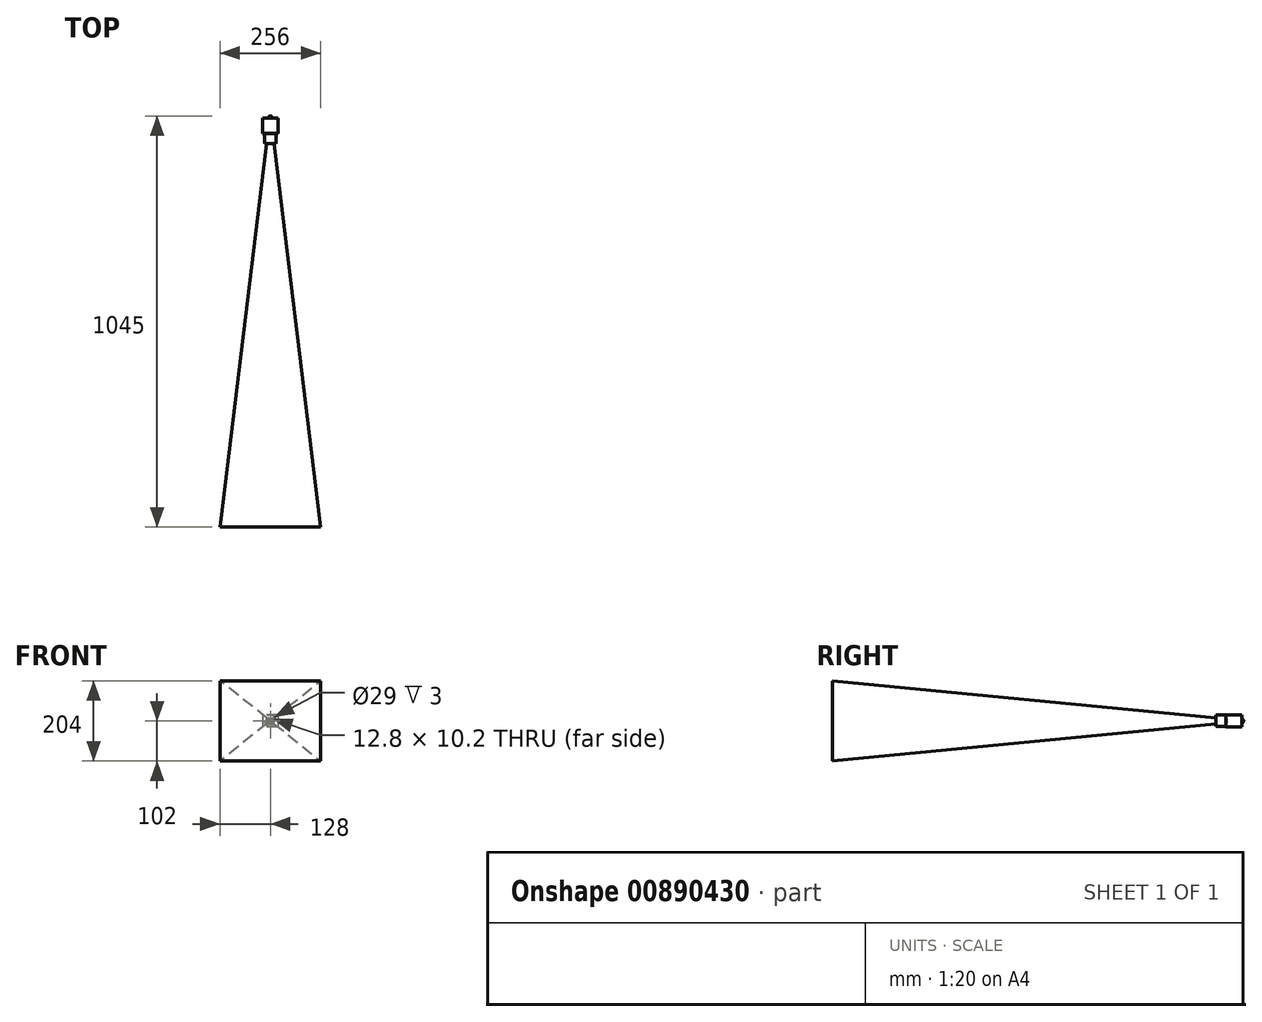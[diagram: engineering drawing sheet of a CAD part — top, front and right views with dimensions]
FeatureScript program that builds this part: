
annotation { "Feature Type Name" : "Feature", "Feature Type Description" : "" }
export const myFeature = defineFeature(function(context is Context, id is Id, definition is map)
    precondition{}
    {
        {
            var Q0;
            Q0=qCreatedBy(makeId("Front.planeOp"),FACE);
            var sketch = newSketch(context, id + "F0", { "sketchPlane" : qUnion([Q0])});
            skLineSegment(sketch, "E0.bottom", {"start": v(20, 15) * mm, "end": v(-20, 15) * mm});
            skLineSegment(sketch, "E0.top", {"start": v(20, -15) * mm, "end": v(-20, -15) * mm});
            skLineSegment(sketch, "E0.left", {"start": v(20, 15) * mm, "end": v(20, -15) * mm});
            skLineSegment(sketch, "E0.right", {"start": v(-20, 15) * mm, "end": v(-20, -15) * mm});
            skPoint(sketch, "E0.middle", {"position": v(0, 0) * mm});
            skSolve(sketch);
        }
        {
            var Q0;
            Q0=qSketchRegion(id+"F0",true);
            extrude(context, id + "F1", {"entities" : qUnion([Q0]), "depth" : 40 * mm, "offsetDistance" : 25 * mm});
        }
        {
            assignVariable(context, id + "F2", {"name" : "WorkingDistance", "anyValue" : 1000});
        }
        {
            var Q0;
            Q0=makeQuery(id+"F1.opExtrude","CAP_FACE",FACE,{"disambiguationData":[OSD([sQuery(id+"F0.wireOp",EDGE,"E0.bottom"),sQuery(id+"F0.wireOp",EDGE,"E0.top"),sQuery(id+"F0.wireOp",EDGE,"E0.left"),sQuery(id+"F0.wireOp",EDGE,"E0.right")])],"isStart":false});
            var sketch = newSketch(context, id + "F3", { "sketchPlane" : qUnion([Q0])});
            skCircle(sketch, "E1", {"center": v(0, 0) * mm, "radius": 14.5 * mm});
            skSolve(sketch);
        }
        {
            var Q0;
            Q0=qSketchRegion(id+"F3",true);
            extrude(context, id + "F4", {"entities" : qUnion([Q0]), "operationType" : NewBodyOperationType.REMOVE, "oppositeDirection" : true, "depth" : 3 * mm, "offsetDistance" : 25 * mm});
        }
        {
            var Q0;
            Q0=makeQuery(id+"F4.boolean.opBoolean","COPY",FACE,{"derivedFrom":makeQuery(id+"F4.opExtrude","CAP_FACE",FACE,{"disambiguationData":[OSD([sQuery(id+"F3.wireOp",EDGE,"E1")])],"isStart":false})});
            var sketch = newSketch(context, id + "F5", { "sketchPlane" : qUnion([Q0])});
            skLineSegment(sketch, "E2.bottom", {"start": v(6.4, 5.1) * mm, "end": v(-6.4, 5.1) * mm});
            skLineSegment(sketch, "E2.top", {"start": v(6.4, -5.1) * mm, "end": v(-6.4, -5.1) * mm});
            skLineSegment(sketch, "E2.left", {"start": v(6.4, 5.1) * mm, "end": v(6.4, -5.1) * mm});
            skLineSegment(sketch, "E2.right", {"start": v(-6.4, 5.1) * mm, "end": v(-6.4, -5.1) * mm});
            skPoint(sketch, "E2.middle", {"position": v(0, 0) * mm});
            skSolve(sketch);
        }
        {
            var Q0;
            Q0=qSketchRegion(id+"F5",true);
            extrude(context, id + "F6", {"entities" : qUnion([Q0]), "operationType" : NewBodyOperationType.ADD, "depth" : 3 * mm, "offsetDistance" : 25 * mm});
        }
        {
            var Q0;
            Q0=makeQuery(id+"F6.opExtrude","CAP_FACE",FACE,{"disambiguationData":[OSD([sQuery(id+"F5.wireOp",EDGE,"E2.bottom"),sQuery(id+"F5.wireOp",EDGE,"E2.top"),sQuery(id+"F5.wireOp",EDGE,"E2.left"),sQuery(id+"F5.wireOp",EDGE,"E2.right")])],"isStart":false});
            cPlane(context, id + "F7", {"entities" : qUnion([Q0]), "cplaneType" : CPlaneType.OFFSET, "offset" : (getVariable(context, 'WorkingDistance')) * mm, "width" : 150 * mm, "height" : 150 * mm});
        }
        {
            var Q0;
            Q0=qCreatedBy(id+"F7.planeOp",FACE);
            var sketch = newSketch(context, id + "F8", { "sketchPlane" : qUnion([Q0])});
            skLineSegment(sketch, "E3.bottom", {"start": v(128, 102) * mm, "end": v(-128, 102) * mm});
            skLineSegment(sketch, "E3.top", {"start": v(128, -102) * mm, "end": v(-128, -102) * mm});
            skLineSegment(sketch, "E3.left", {"start": v(128, 102) * mm, "end": v(128, -102) * mm});
            skLineSegment(sketch, "E3.right", {"start": v(-128, 102) * mm, "end": v(-128, -102) * mm});
            skPoint(sketch, "E3.middle", {"position": v(0, 0) * mm});
            skSolve(sketch);
        }
        {
            var Q1;
            Q1=makeQuery(id+"F6.opExtrude","CAP_FACE",FACE,{"disambiguationData":[OSD([sQuery(id+"F5.wireOp",EDGE,"E2.bottom"),sQuery(id+"F5.wireOp",EDGE,"E2.top"),sQuery(id+"F5.wireOp",EDGE,"E2.left"),sQuery(id+"F5.wireOp",EDGE,"E2.right")])],"isStart":false});
            var Q2;
            Q2=makeQuery(id+"F8.imprint","IMPRINT",FACE,{"disambiguationData":[TD([[makeQuery(id+"F8.imprint","IMPRINT",EDGE,{"derivedFrom":sQuery(id+"F8.wireOp",EDGE,"E3.bottom")}),1.0]])]});
            loft(context, id + "F9", {"operationType" : NewBodyOperationType.ADD, "sheetProfilesArray" : [{ "sheetProfileEntities" : qUnion([Q1]) }, { "sheetProfileEntities" : qUnion([Q2]) }]});
        }
        {
            var Q0;
            Q0=makeQuery(id+"F0.imprint","IMPRINT",FACE,{"disambiguationData":[TD([[makeQuery(id+"F0.imprint","IMPRINT",EDGE,{"derivedFrom":sQuery(id+"F0.wireOp",EDGE,"E0.bottom")}),1.0]])]});
            var sketch = newSketch(context, id + "F10", { "sketchPlane" : qUnion([Q0])});
            skArc(sketch, "E4", {"start": v(0, 5) * mm, "mid": v(5, 0) * mm, "end": v(0, -5) * mm});
            skLineSegment(sketch, "E5", {"start": v(0, 5) * mm, "end": v(0, -5) * mm});
            skSolve(sketch);
        }
        {
            var Q0;
            Q0=qSketchRegion(id+"F10",true);
            var Q1;
            Q1=sQuery(id+"F10.wireOp",EDGE,"E5");
            revolve(context, id + "F11", {"operationType" : NewBodyOperationType.ADD, "surfaceOperationType" : NewSurfaceOperationType.NEW, "entities" : qUnion([Q0]), "axis" : qUnion([Q1]), "revolveType" : RevolveType.FULL});
        }
        {
            var Q0;
            Q0=makeQuery(id+"F1.opExtrude","CAP_FACE",FACE,{"disambiguationData":[OSD([sQuery(id+"F0.wireOp",EDGE,"E0.bottom"),sQuery(id+"F0.wireOp",EDGE,"E0.top"),sQuery(id+"F0.wireOp",EDGE,"E0.left"),sQuery(id+"F0.wireOp",EDGE,"E0.right")])],"isStart":false});
            var sketch = newSketch(context, id + "F12", { "sketchPlane" : qUnion([Q0])});
            skCircle(sketch, "E6", {"center": v(0, 0) * mm, "radius": 14.74 * mm});
            skSolve(sketch);
        }
        {
            var Q0;
            Q0 = qSketchRegion(id + "F12", true);
            extrude(context, id + "F13", {"entities" : qUnion([Q0]), "operationType" : NewBodyOperationType.ADD, "depth" : 25 * mm, "offsetDistance" : 25 * mm});
        }
    });
